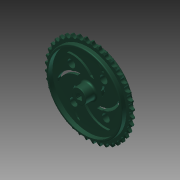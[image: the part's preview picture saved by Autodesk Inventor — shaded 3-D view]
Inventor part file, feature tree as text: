
AUTODESK INVENTOR PART (.ipt)
format: ipt  version: 2013 (Build 170138000, 138)  size: 3,260,928 bytes
history: native  units: mm (DEFAULTED — no unit token found)
features: imported_body x1, sketch x1, other x1, extrude x1
ambient origin geometry x8: Origin, YZ Plane, XZ Plane, XY Plane, X Axis, Y Axis, Z Axis, Center Point
bodies: Solid1 (feature_tree)
feature tree (4):
  imported_body  "Base1"
  sketch  "Sketch1"  dims[d1=2.2606mm d5=25.4mm d6=0.0mm d7=0.0mm d8=0.0mm]
  other  "Srf1"
  extrude  "ExtrusionSrf1"  Depth=25.4mm TaperAngle=0.0deg
